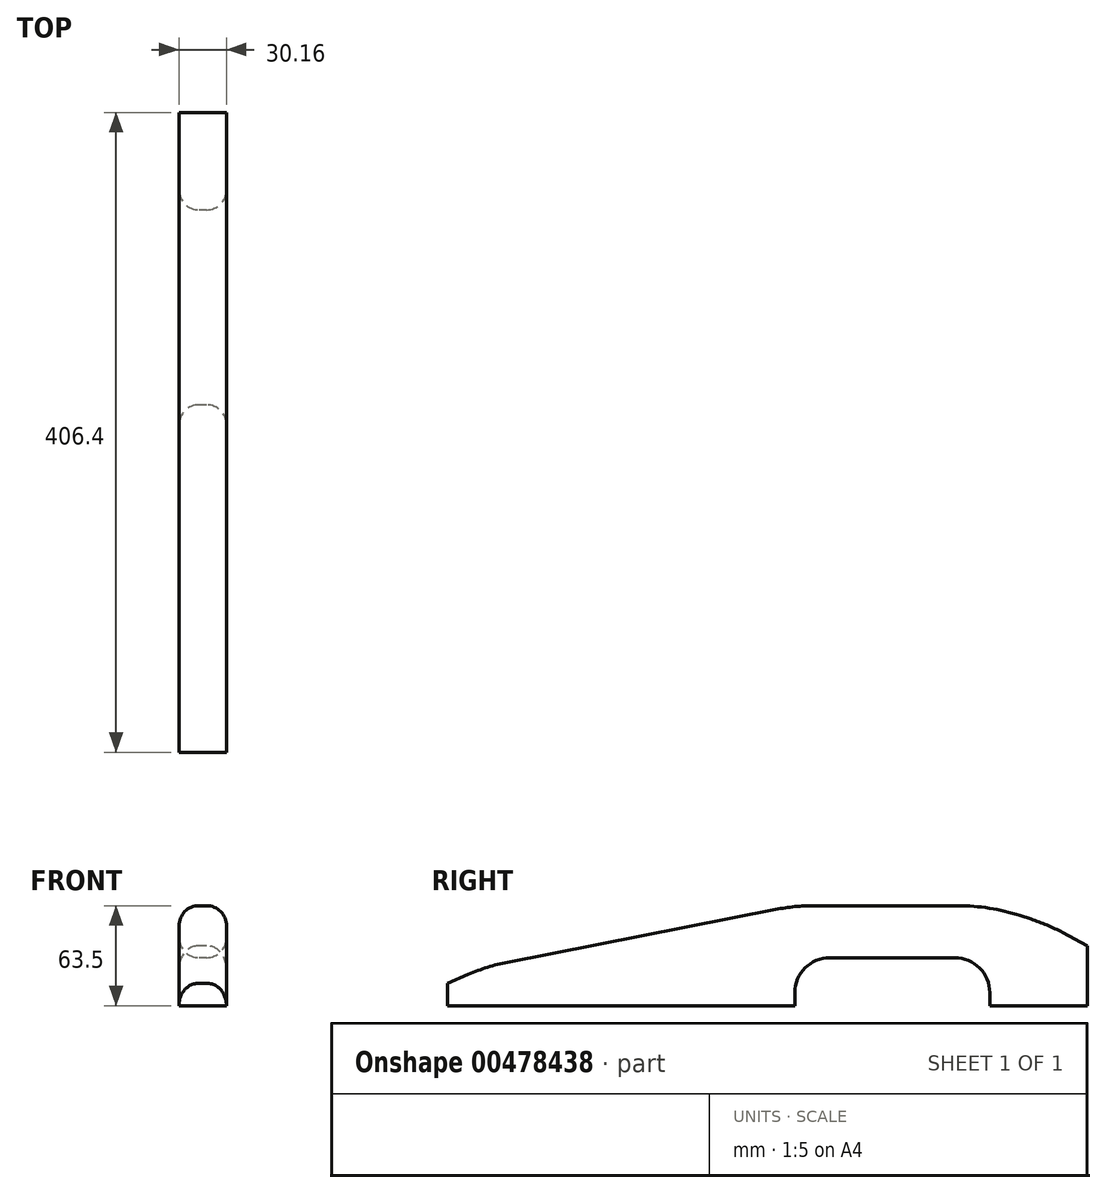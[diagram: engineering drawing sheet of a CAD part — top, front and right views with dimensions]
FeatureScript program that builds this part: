
annotation { "Feature Type Name" : "Feature", "Feature Type Description" : "" }
export const myFeature = defineFeature(function(context is Context, id is Id, definition is map)
    precondition{}
    {
        {
            var Q0;
            Q0=qCreatedBy(makeId("Right.planeOp"),FACE);
            var sketch = newSketch(context, id + "F0", { "sketchPlane" : qUnion([Q0])});
            skLineSegment(sketch, "E0.bottom", {"start": v(0, 0) * mm, "end": v(220.66, 0) * mm});
            skLineSegment(sketch, "E0.top", {"start": v(220.66, 63.5) * mm, "end": v(344.49, 63.5) * mm});
            skLineSegment(sketch, "E0.left", {"start": v(0, 0) * mm, "end": v(0, 14.29) * mm});
            skLineSegment(sketch, "E0.right", {"start": v(406.4, 0) * mm, "end": v(406.4, 38.1) * mm});
            skPoint(sketch, "E1", {"position": v(220.66, 0) * mm});
            skPoint(sketch, "E2", {"position": v(344.49, 0) * mm});
            skPoint(sketch, "E3", {"position": v(406.4, 38.1) * mm});
            skPoint(sketch, "E4", {"position": v(0, 14.29) * mm});
            skLineSegment(sketch, "E5", {"start": v(220.66, 0) * mm, "end": v(220.66, 30.48) * mm});
            skLineSegment(sketch, "E6", {"start": v(220.66, 30.48) * mm, "end": v(344.49, 30.48) * mm});
            skLineSegment(sketch, "E7", {"start": v(344.49, 30.48) * mm, "end": v(344.49, 0) * mm});
            skLineSegment(sketch, "E8.trimOffspring", {"start": v(344.49, 0) * mm, "end": v(406.4, 0) * mm});
            skLineSegment(sketch, "E9", {"start": v(0, 14.29) * mm, "end": v(25.4, 25.07) * mm});
            skLineSegment(sketch, "E10", {"start": v(25.4, 25.07) * mm, "end": v(220.66, 63.5) * mm});
            skLineSegment(sketch, "E11", {"start": v(406.4, 38.1) * mm, "end": v(381, 51.6) * mm});
            skLineSegment(sketch, "E12", {"start": v(381, 51.6) * mm, "end": v(344.49, 63.5) * mm});
            skSolve(sketch);
        }
        {
            var Q0;
            Q0=makeQuery(id+"F0.imprint","IMPRINT",FACE,{"disambiguationData":[TD([[makeQuery(id+"F0.imprint","IMPRINT",EDGE,{"derivedFrom":sQuery(id+"F0.wireOp",EDGE,"E0.bottom")}),1.0]])]});
            extrude(context, id + "F1", {"entities" : qUnion([Q0]), "depth" : 15.08 * mm, "hasSecondDirection" : true, "secondDirectionOppositeDirection" : true, "secondDirectionDepth" : 15.08 * mm});
        }
        {
            var Q0;
            Q0=makeQuery(id+"F1.opExtrude","SWEPT_EDGE",EDGE,{"disambiguationData":[OSD([sQuery(id+"F0.wireOp",EDGE,"E9"),sQuery(id+"F0.wireOp",EDGE,"E10")])]});
            var Q1;
            Q1=makeQuery(id+"F1.opExtrude","SWEPT_EDGE",EDGE,{"disambiguationData":[OSD([sQuery(id+"F0.wireOp",EDGE,"E11"),sQuery(id+"F0.wireOp",EDGE,"E12")])]});
            var Q2;
            Q2=makeQuery(id+"F1.opExtrude","SWEPT_EDGE",EDGE,{"disambiguationData":[OSD([sQuery(id+"F0.wireOp",EDGE,"E0.top"),sQuery(id+"F0.wireOp",EDGE,"E12")])]});
            var Q3;
            Q3=makeQuery(id+"F1.opExtrude","SWEPT_EDGE",EDGE,{"disambiguationData":[OSD([sQuery(id+"F0.wireOp",EDGE,"E0.top"),sQuery(id+"F0.wireOp",EDGE,"E10")])]});
            fillet(context, id + "F2", {"entities" : qUnion([Q0, Q1, Q2, Q3]), "radius" : 127 * mm, "tangentPropagation" : true, "allowEdgeOverflow" : false});
        }
        {
            var Q0;
            Q0=makeQuery(id+"F1.opExtrude","SWEPT_EDGE",EDGE,{"disambiguationData":[OSD([sQuery(id+"F0.wireOp",EDGE,"E5"),sQuery(id+"F0.wireOp",EDGE,"E6")])]});
            var Q1;
            Q1=makeQuery(id+"F1.opExtrude","SWEPT_EDGE",EDGE,{"disambiguationData":[OSD([sQuery(id+"F0.wireOp",EDGE,"E6"),sQuery(id+"F0.wireOp",EDGE,"E7")])]});
            fillet(context, id + "F3", {"entities" : qUnion([Q0, Q1]), "radius" : 22.22 * mm, "tangentPropagation" : true, "allowEdgeOverflow" : false});
        }
        {
            var Q0;
            Q0=makeQuery(id+"F1.opExtrude","CAP_EDGE",EDGE,{"disambiguationData":[OSD([sQuery(id+"F0.wireOp",EDGE,"E6")])],"isStart":false});
            var Q1;
            Q1=makeQuery(id+"F1.opExtrude","CAP_EDGE",EDGE,{"disambiguationData":[OSD([sQuery(id+"F0.wireOp",EDGE,"E0.top")])],"isStart":false});
            var Q2;
            Q2=makeQuery(id+"F1.opExtrude","CAP_EDGE",EDGE,{"disambiguationData":[OSD([sQuery(id+"F0.wireOp",EDGE,"E0.top")])],"isStart":true});
            var Q3;
            Q3=makeQuery(id+"F1.opExtrude","CAP_EDGE",EDGE,{"disambiguationData":[OSD([sQuery(id+"F0.wireOp",EDGE,"E6")])],"isStart":true});
            fillet(context, id + "F4", {"entities" : qUnion([Q0, Q1, Q2, Q3]), "radius" : 12.7 * mm, "tangentPropagation" : true, "allowEdgeOverflow" : false});
        }
    });
